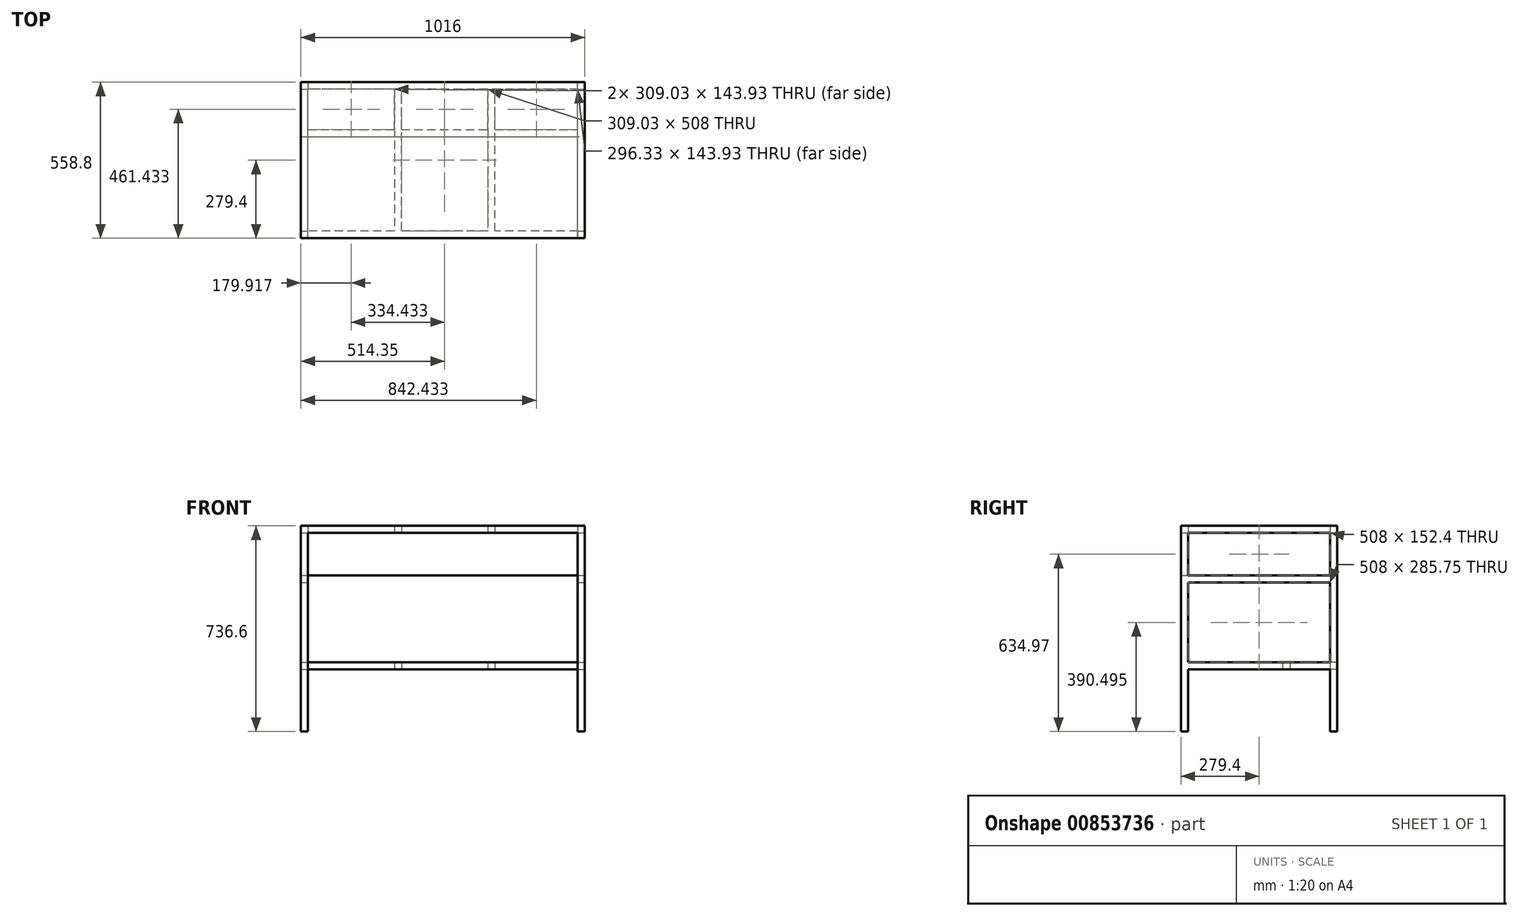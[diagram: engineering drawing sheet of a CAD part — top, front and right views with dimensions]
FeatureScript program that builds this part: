
annotation { "Feature Type Name" : "Feature", "Feature Type Description" : "" }
export const myFeature = defineFeature(function(context is Context, id is Id, definition is map)
    precondition{}
    {
        {
            assignVariable(context, id + "F0", {"name" : "width", "anyValue" : 1016 * mm});
        }
        {
            assignVariable(context, id + "F1", {"name" : "height", "anyValue" : 736.6 * mm});
        }
        {
            assignVariable(context, id + "F2", {"name" : "beam", "anyValue" : 25.4 * mm});
        }
        {
            assignVariable(context, id + "F3", {"name" : "ply", "anyValue" : 3 / 101.6 * mm});
        }
        {
            var Q0;
            Q0=qCreatedBy(makeId("Top.planeOp"),FACE);
            var sketch = newSketch(context, id + "F4", { "sketchPlane" : qUnion([Q0])});
            skLineSegment(sketch, "E0.bottom", {"start": v(508, -279.4) * mm, "end": v(-508, -279.4) * mm});
            skLineSegment(sketch, "E0.top", {"start": v(508, 279.4) * mm, "end": v(-508, 279.4) * mm});
            skLineSegment(sketch, "E0.left", {"start": v(508, -279.4) * mm, "end": v(508, 279.4) * mm});
            skLineSegment(sketch, "E0.right", {"start": v(-508, -279.4) * mm, "end": v(-508, 279.4) * mm});
            skPoint(sketch, "E0.middle", {"position": v(0, 0) * mm});
            skLineSegment(sketch, "E1.bottom", {"start": v(482.6, -254) * mm, "end": v(-482.6, -254) * mm});
            skLineSegment(sketch, "E1.top", {"start": v(482.6, 254) * mm, "end": v(-482.6, 254) * mm});
            skLineSegment(sketch, "E1.left", {"start": v(482.6, -254) * mm, "end": v(482.6, 254) * mm});
            skLineSegment(sketch, "E1.right", {"start": v(-482.6, -254) * mm, "end": v(-482.6, 254) * mm});
            skLineSegment(sketch, "E2", {"start": v(-173.57, 254) * mm, "end": v(-173.57, -254) * mm});
            skLineSegment(sketch, "E3", {"start": v(-173.57, -254) * mm, "end": v(-148.17, -254) * mm});
            skLineSegment(sketch, "E4", {"start": v(-148.17, -254) * mm, "end": v(-148.17, 254) * mm});
            skLineSegment(sketch, "E5", {"start": v(-148.17, 254) * mm, "end": v(-173.57, 254) * mm});
            skLineSegment(sketch, "E6", {"start": v(160.87, 254) * mm, "end": v(160.87, -254) * mm});
            skLineSegment(sketch, "E7", {"start": v(160.87, -254) * mm, "end": v(186.27, -254) * mm});
            skLineSegment(sketch, "E8", {"start": v(186.27, -254) * mm, "end": v(186.27, 254) * mm});
            skLineSegment(sketch, "E9", {"start": v(186.27, 254) * mm, "end": v(160.87, 254) * mm});
            skSolve(sketch);
        }
        {
            var Q0;
            Q0=makeQuery(id+"F4.imprint","IMPRINT",FACE,{"disambiguationData":[TD([[makeQuery(id+"F4.imprint","IMPRINT",EDGE,{"derivedFrom":sQuery(id+"F4.wireOp",EDGE,"E0.right")}),-1.0]])]});
            var Q1;
            Q1=makeQuery(id+"F4.imprint","IMPRINT",FACE,{"disambiguationData":[TD([[makeQuery(id+"F4.imprint","IMPRINT",EDGE,{"derivedFrom":sQuery(id+"F4.wireOp",EDGE,"E0.bottom")}),-1.0]])]});
            var Q2;
            Q2=makeQuery(id+"F4.imprint","IMPRINT",FACE,{"disambiguationData":[TD([[makeQuery(id+"F4.imprint","IMPRINT",EDGE,{"derivedFrom":sQuery(id+"F4.wireOp",EDGE,"E0.top")}),1.0]])]});
            var Q3;
            Q3=makeQuery(id+"F4.imprint","IMPRINT",FACE,{"disambiguationData":[TD([[makeQuery(id+"F4.imprint","IMPRINT",EDGE,{"derivedFrom":sQuery(id+"F4.wireOp",EDGE,"E0.left")}),1.0]])]});
            var Q4;
            Q4=makeQuery(id+"F4.imprint","IMPRINT",FACE,{"disambiguationData":[TD([[makeQuery(id+"F4.imprint","IMPRINT",EDGE,{"derivedFrom":sQuery(id+"F4.wireOp",EDGE,"E2")}),1.0]])]});
            var Q5;
            Q5=makeQuery(id+"F4.imprint","IMPRINT",FACE,{"disambiguationData":[TD([[makeQuery(id+"F4.imprint","IMPRINT",EDGE,{"derivedFrom":sQuery(id+"F4.wireOp",EDGE,"E6")}),1.0]])]});
            extrude(context, id + "F5", {"entities" : qUnion([Q0, Q1, Q2, Q3, Q4, Q5]), "depth" : getVariable(context, 'beam'), "offsetDistance" : 25.4 * mm});
        }
        {
            var Q0;
            Q0=makeQuery(id+"F5.opExtrude","CAP_FACE",FACE,{"disambiguationData":[OSD([sQuery(id+"F4.wireOp",EDGE,"E0.bottom"),sQuery(id+"F4.wireOp",EDGE,"E0.top"),sQuery(id+"F4.wireOp",EDGE,"E0.left"),sQuery(id+"F4.wireOp",EDGE,"E0.right"),sQuery(id+"F4.wireOp",EDGE,"E1.bottom"),sQuery(id+"F4.wireOp",EDGE,"E1.top"),sQuery(id+"F4.wireOp",EDGE,"E1.left"),sQuery(id+"F4.wireOp",EDGE,"E1.right")])],"isStart":false});
            var sketch = newSketch(context, id + "F6", { "sketchPlane" : qUnion([Q0])});
            skLineSegment(sketch, "E10.bottom", {"start": v(-508, 279.4) * mm, "end": v(508, 279.4) * mm});
            skLineSegment(sketch, "E10.top", {"start": v(-508, -279.4) * mm, "end": v(508, -279.4) * mm});
            skLineSegment(sketch, "E10.left", {"start": v(-508, 279.4) * mm, "end": v(-508, -279.4) * mm});
            skLineSegment(sketch, "E10.right", {"start": v(508, 279.4) * mm, "end": v(508, -279.4) * mm});
            skSolve(sketch);
        }
        {
            var Q0;
            Q0 = qSketchRegion(id + "F6", true);
            extrude(context, id + "F7", {"entities" : qUnion([Q0]), "depth" : getVariable(context, 'ply'), "offsetDistance" : 25.4 * mm});
        }
        {
            var Q0;
            Q0=makeQuery(id+"F5.opExtrude","CAP_FACE",FACE,{"disambiguationData":[OSD([sQuery(id+"F4.wireOp",EDGE,"E0.bottom"),sQuery(id+"F4.wireOp",EDGE,"E0.top"),sQuery(id+"F4.wireOp",EDGE,"E0.left"),sQuery(id+"F4.wireOp",EDGE,"E0.right"),sQuery(id+"F4.wireOp",EDGE,"E1.bottom"),sQuery(id+"F4.wireOp",EDGE,"E1.top"),sQuery(id+"F4.wireOp",EDGE,"E1.left"),sQuery(id+"F4.wireOp",EDGE,"E1.right"),sQuery(id+"F4.wireOp",EDGE,"E2"),sQuery(id+"F4.wireOp",EDGE,"E4"),sQuery(id+"F4.wireOp",EDGE,"E6"),sQuery(id+"F4.wireOp",EDGE,"E8")])],"isStart":true});
            var sketch = newSketch(context, id + "F8", { "sketchPlane" : qUnion([Q0])});
            skLineSegment(sketch, "E11.bottom", {"start": v(-508, 279.4) * mm, "end": v(-482.6, 279.4) * mm});
            skLineSegment(sketch, "E11.top", {"start": v(-508, 254) * mm, "end": v(-482.6, 254) * mm});
            skLineSegment(sketch, "E11.left", {"start": v(-508, 279.4) * mm, "end": v(-508, 254) * mm});
            skLineSegment(sketch, "E11.right", {"start": v(-482.6, 279.4) * mm, "end": v(-482.6, 254) * mm});
            skLineSegment(sketch, "E12.bottom", {"start": v(-508, -279.4) * mm, "end": v(-482.6, -279.4) * mm});
            skLineSegment(sketch, "E12.top", {"start": v(-508, -254) * mm, "end": v(-482.6, -254) * mm});
            skLineSegment(sketch, "E12.left", {"start": v(-508, -279.4) * mm, "end": v(-508, -254) * mm});
            skLineSegment(sketch, "E12.right", {"start": v(-482.6, -279.4) * mm, "end": v(-482.6, -254) * mm});
            skLineSegment(sketch, "E13.bottom", {"start": v(482.6, 254) * mm, "end": v(508, 254) * mm});
            skLineSegment(sketch, "E13.top", {"start": v(482.6, 279.4) * mm, "end": v(508, 279.4) * mm});
            skLineSegment(sketch, "E13.left", {"start": v(482.6, 254) * mm, "end": v(482.6, 279.4) * mm});
            skLineSegment(sketch, "E13.right", {"start": v(508, 254) * mm, "end": v(508, 279.4) * mm});
            skLineSegment(sketch, "E14.bottom", {"start": v(482.6, -254) * mm, "end": v(508, -254) * mm});
            skLineSegment(sketch, "E14.top", {"start": v(482.6, -279.4) * mm, "end": v(508, -279.4) * mm});
            skLineSegment(sketch, "E14.left", {"start": v(482.6, -254) * mm, "end": v(482.6, -279.4) * mm});
            skLineSegment(sketch, "E14.right", {"start": v(508, -254) * mm, "end": v(508, -279.4) * mm});
            skSolve(sketch);
        }
        {
            var Q0;
            Q0 = qSketchRegion(id + "F8", true);
            extrude(context, id + "F9", {"entities" : qUnion([Q0]), "operationType" : NewBodyOperationType.ADD, "depth" : getVariable(context, 'height') - getVariable(context, 'beam') - getVariable(context, 'ply'), "offsetDistance" : 25.4 * mm});
        }
        {
            var Q0;
            Q0=makeQuery(id+"F9.opExtrude","SWEPT_FACE",FACE,{"disambiguationData":[OSD([sQuery(id+"F8.wireOp",EDGE,"E12.top")])]});
            var sketch = newSketch(context, id + "F10", { "sketchPlane" : qUnion([Q0])});
            skLineSegment(sketch, "E15.bottom", {"start": v(-508, -463.55) * mm, "end": v(-482.6, -463.55) * mm});
            skLineSegment(sketch, "E15.top", {"start": v(-508, -488.95) * mm, "end": v(-482.6, -488.95) * mm});
            skLineSegment(sketch, "E15.left", {"start": v(-508, -463.55) * mm, "end": v(-508, -488.95) * mm});
            skLineSegment(sketch, "E15.right", {"start": v(-482.6, -463.55) * mm, "end": v(-482.6, -488.95) * mm});
            skSolve(sketch);
        }
        {
            var Q0;
            Q0=makeQuery(id+"F10.imprint","IMPRINT",FACE,{"disambiguationData":[TD([[makeQuery(id+"F10.imprint","IMPRINT",EDGE,{"derivedFrom":sQuery(id+"F10.wireOp",EDGE,"E15.bottom")}),-1.0]])]});
            extrude(context, id + "F11", {"entities" : qUnion([Q0]), "operationType" : NewBodyOperationType.ADD, "endBound" : BoundingType.UP_TO_NEXT, "depth" : 25.4 * mm, "offsetDistance" : 25.4 * mm});
        }
        {
            var Q0;
            Q0=makeQuery(id+"F9.opExtrude","SWEPT_FACE",FACE,{"disambiguationData":[OSD([sQuery(id+"F8.wireOp",EDGE,"E14.bottom")])]});
            var sketch = newSketch(context, id + "F12", { "sketchPlane" : qUnion([Q0])});
            skLineSegment(sketch, "E16.bottom", {"start": v(482.6, -463.55) * mm, "end": v(508, -463.55) * mm});
            skLineSegment(sketch, "E16.top", {"start": v(482.6, -488.95) * mm, "end": v(508, -488.95) * mm});
            skLineSegment(sketch, "E16.left", {"start": v(482.6, -463.55) * mm, "end": v(482.6, -488.95) * mm});
            skLineSegment(sketch, "E16.right", {"start": v(508, -463.55) * mm, "end": v(508, -488.95) * mm});
            skSolve(sketch);
        }
        {
            var Q0;
            Q0=makeQuery(id+"F12.imprint","IMPRINT",FACE,{"disambiguationData":[TD([[makeQuery(id+"F12.imprint","IMPRINT",EDGE,{"derivedFrom":sQuery(id+"F12.wireOp",EDGE,"E16.bottom")}),-1.0]])]});
            extrude(context, id + "F13", {"entities" : qUnion([Q0]), "operationType" : NewBodyOperationType.ADD, "endBound" : BoundingType.UP_TO_NEXT, "depth" : 25.4 * mm, "offsetDistance" : 25.4 * mm});
        }
        {
            var Q0;
            Q0=makeQuery(id+"F13.boolean.opBoolean","MERGE",FACE,{"derivedFrom":[makeQuery(id+"F9.opExtrude","SWEPT_FACE",FACE,{"disambiguationData":[OSD([sQuery(id+"F8.wireOp",EDGE,"E13.left")])]}),makeQuery(id+"F9.opExtrude","SWEPT_FACE",FACE,{"disambiguationData":[OSD([sQuery(id+"F8.wireOp",EDGE,"E14.left")])]}),makeQuery(id+"F13.opExtrude","SWEPT_FACE",FACE,{"disambiguationData":[OSD([sQuery(id+"F12.wireOp",EDGE,"E16.left")])]})]});
            var sketch = newSketch(context, id + "F14", { "sketchPlane" : qUnion([Q0])});
            skLineSegment(sketch, "E17.bottom", {"start": v(-110.07, -463.55) * mm, "end": v(-84.67, -463.55) * mm});
            skLineSegment(sketch, "E17.top", {"start": v(-110.07, -488.95) * mm, "end": v(-84.67, -488.95) * mm});
            skLineSegment(sketch, "E17.left", {"start": v(-110.07, -463.55) * mm, "end": v(-110.07, -488.95) * mm});
            skLineSegment(sketch, "E17.right", {"start": v(-84.67, -463.55) * mm, "end": v(-84.67, -488.95) * mm});
            skLineSegment(sketch, "E18.bottom", {"start": v(-254, -463.55) * mm, "end": v(-279.4, -463.55) * mm});
            skLineSegment(sketch, "E18.top", {"start": v(-254, -488.95) * mm, "end": v(-279.4, -488.95) * mm});
            skLineSegment(sketch, "E18.left", {"start": v(-254, -463.55) * mm, "end": v(-254, -488.95) * mm});
            skLineSegment(sketch, "E18.right", {"start": v(-279.4, -463.55) * mm, "end": v(-279.4, -488.95) * mm});
            skSolve(sketch);
        }
        {
            var Q0;
            Q0=makeQuery(id+"F14.imprint","IMPRINT",FACE,{"disambiguationData":[TD([[makeQuery(id+"F14.imprint","IMPRINT",EDGE,{"derivedFrom":sQuery(id+"F14.wireOp",EDGE,"E17.bottom")}),1.0]])]});
            var Q1;
            Q1=makeQuery(id+"F14.imprint","IMPRINT",FACE,{"disambiguationData":[TD([[makeQuery(id+"F14.imprint","IMPRINT",EDGE,{"derivedFrom":sQuery(id+"F14.wireOp",EDGE,"E18.bottom")}),1.0]])]});
            extrude(context, id + "F15", {"entities" : qUnion([Q0, Q1]), "operationType" : NewBodyOperationType.ADD, "endBound" : BoundingType.UP_TO_NEXT, "depth" : 25.4 * mm, "offsetDistance" : 25.4 * mm});
        }
        {
            var Q0;
            Q0=makeQuery(id+"F15.opExtrude","SWEPT_FACE",FACE,{"disambiguationData":[OSD([sQuery(id+"F14.wireOp",EDGE,"E18.left")])]});
            var sketch = newSketch(context, id + "F16", { "sketchPlane" : qUnion([Q0])});
            skLineSegment(sketch, "E19.bottom", {"start": v(-173.57, -463.55) * mm, "end": v(-148.17, -463.55) * mm});
            skLineSegment(sketch, "E19.top", {"start": v(-173.57, -488.95) * mm, "end": v(-148.17, -488.95) * mm});
            skLineSegment(sketch, "E19.left", {"start": v(-173.57, -463.55) * mm, "end": v(-173.57, -488.95) * mm});
            skLineSegment(sketch, "E19.right", {"start": v(-148.17, -463.55) * mm, "end": v(-148.17, -488.95) * mm});
            skLineSegment(sketch, "E20.bottom", {"start": v(160.87, -463.55) * mm, "end": v(186.27, -463.55) * mm});
            skLineSegment(sketch, "E20.top", {"start": v(160.87, -488.95) * mm, "end": v(186.27, -488.95) * mm});
            skLineSegment(sketch, "E20.left", {"start": v(160.87, -463.55) * mm, "end": v(160.87, -488.95) * mm});
            skLineSegment(sketch, "E20.right", {"start": v(186.27, -463.55) * mm, "end": v(186.27, -488.95) * mm});
            skSolve(sketch);
        }
        {
            var Q0;
            Q0=makeQuery(id+"F16.imprint","IMPRINT",FACE,{"disambiguationData":[TD([[makeQuery(id+"F16.imprint","IMPRINT",EDGE,{"derivedFrom":sQuery(id+"F16.wireOp",EDGE,"E19.bottom")}),-1.0]])]});
            var Q1;
            Q1=makeQuery(id+"F16.imprint","IMPRINT",FACE,{"disambiguationData":[TD([[makeQuery(id+"F16.imprint","IMPRINT",EDGE,{"derivedFrom":sQuery(id+"F16.wireOp",EDGE,"E20.bottom")}),-1.0]])]});
            extrude(context, id + "F17", {"entities" : qUnion([Q0, Q1]), "operationType" : NewBodyOperationType.ADD, "endBound" : BoundingType.UP_TO_NEXT, "depth" : 25.4 * mm, "offsetDistance" : 25.4 * mm});
        }
        {
            var Q0;
            Q0=makeQuery(id+"F17.boolean.opBoolean","MERGE",FACE,{"derivedFrom":[makeQuery(id+"F15.opExtrude","SWEPT_FACE",FACE,{"disambiguationData":[OSD([sQuery(id+"F14.wireOp",EDGE,"E18.bottom")])]}),makeQuery(id+"F15.boolean.opBoolean","MERGE",FACE,{"derivedFrom":[makeQuery(id+"F11.opExtrude","SWEPT_FACE",FACE,{"disambiguationData":[OSD([sQuery(id+"F10.wireOp",EDGE,"E15.bottom")])]}),makeQuery(id+"F13.opExtrude","SWEPT_FACE",FACE,{"disambiguationData":[OSD([sQuery(id+"F12.wireOp",EDGE,"E16.bottom")])]}),makeQuery(id+"F15.opExtrude","SWEPT_FACE",FACE,{"disambiguationData":[OSD([sQuery(id+"F14.wireOp",EDGE,"E17.bottom")])]})]}),makeQuery(id+"F17.opExtrude","SWEPT_FACE",FACE,{"disambiguationData":[OSD([sQuery(id+"F16.wireOp",EDGE,"E19.bottom")])]}),makeQuery(id+"F17.opExtrude","SWEPT_FACE",FACE,{"disambiguationData":[OSD([sQuery(id+"F16.wireOp",EDGE,"E20.bottom")])]})]});
            var sketch = newSketch(context, id + "F18", { "sketchPlane" : qUnion([Q0])});
            skLineSegment(sketch, "E21", {"start": v(-508, 254) * mm, "end": v(-482.6, 254) * mm});
            skLineSegment(sketch, "E22", {"start": v(-482.6, 254) * mm, "end": v(-482.6, 279.4) * mm});
            skLineSegment(sketch, "E23", {"start": v(-482.6, 279.4) * mm, "end": v(482.6, 279.4) * mm});
            skLineSegment(sketch, "E24", {"start": v(482.6, 279.4) * mm, "end": v(482.6, 254) * mm});
            skLineSegment(sketch, "E25", {"start": v(482.6, 254) * mm, "end": v(508, 254) * mm});
            skLineSegment(sketch, "E26", {"start": v(-508, 254) * mm, "end": v(-508, 84.67) * mm});
            skLineSegment(sketch, "E27", {"start": v(-508, 84.67) * mm, "end": v(508, 84.67) * mm});
            skLineSegment(sketch, "E28", {"start": v(508, 84.67) * mm, "end": v(508, 254) * mm});
            skSolve(sketch);
        }
        {
            var Q0;
            Q0 = qSketchRegion(id + "F18", true);
            extrude(context, id + "F19", {"entities" : qUnion([Q0]), "depth" : getVariable(context, 'ply'), "offsetDistance" : 25.4 * mm});
        }
        {
            var Q0;
            {var subQ0=sQuery(id+"F4.wireOp",EDGE,"E1.right");Q0=makeQuery(id+"F11.boolean.opBoolean","SPLIT",FACE,{"disambiguationData":[TD([makeQuery(id+"F5.opExtrude","SWEPT_FACE",FACE,{"disambiguationData":[OSD([subQ0])]})])],"derivedFrom":makeQuery(id+"F9.opExtrude","SWEPT_FACE",FACE,{"disambiguationData":[OSD([sQuery(id+"F8.wireOp",EDGE,"E12.top")])]})});}
            var sketch = newSketch(context, id + "F20", { "sketchPlane" : qUnion([Q0])});
            skLineSegment(sketch, "E29.bottom", {"start": v(-508, -152.4) * mm, "end": v(-482.6, -152.4) * mm});
            skLineSegment(sketch, "E29.top", {"start": v(-508, -177.8) * mm, "end": v(-482.6, -177.8) * mm});
            skLineSegment(sketch, "E29.left", {"start": v(-508, -152.4) * mm, "end": v(-508, -177.8) * mm});
            skLineSegment(sketch, "E29.right", {"start": v(-482.6, -152.4) * mm, "end": v(-482.6, -177.8) * mm});
            skSolve(sketch);
        }
        {
            var Q0;
            Q0=makeQuery(id+"F20.imprint","IMPRINT",FACE,{"disambiguationData":[TD([[makeQuery(id+"F20.imprint","IMPRINT",EDGE,{"derivedFrom":sQuery(id+"F20.wireOp",EDGE,"E29.bottom")}),-1.0]])]});
            extrude(context, id + "F21", {"entities" : qUnion([Q0]), "operationType" : NewBodyOperationType.ADD, "endBound" : BoundingType.UP_TO_NEXT, "depth" : 25.4 * mm, "offsetDistance" : 25.4 * mm});
        }
        {
            var Q0;
            {var subQ1=sQuery(id+"F4.wireOp",EDGE,"E1.left");Q0=makeQuery(id+"F13.boolean.opBoolean","SPLIT",FACE,{"disambiguationData":[TD([makeQuery(id+"F5.opExtrude","SWEPT_FACE",FACE,{"disambiguationData":[OSD([subQ1])]})])],"derivedFrom":makeQuery(id+"F9.opExtrude","SWEPT_FACE",FACE,{"disambiguationData":[OSD([sQuery(id+"F8.wireOp",EDGE,"E14.bottom")])]})});}
            var sketch = newSketch(context, id + "F22", { "sketchPlane" : qUnion([Q0])});
            skLineSegment(sketch, "E30.bottom", {"start": v(482.6, -152.4) * mm, "end": v(508, -152.4) * mm});
            skLineSegment(sketch, "E30.top", {"start": v(482.6, -177.8) * mm, "end": v(508, -177.8) * mm});
            skLineSegment(sketch, "E30.left", {"start": v(482.6, -152.4) * mm, "end": v(482.6, -177.8) * mm});
            skLineSegment(sketch, "E30.right", {"start": v(508, -152.4) * mm, "end": v(508, -177.8) * mm});
            skSolve(sketch);
        }
        {
            var Q0;
            Q0=makeQuery(id+"F22.imprint","IMPRINT",FACE,{"disambiguationData":[TD([[makeQuery(id+"F22.imprint","IMPRINT",EDGE,{"derivedFrom":sQuery(id+"F22.wireOp",EDGE,"E30.bottom")}),-1.0]])]});
            extrude(context, id + "F23", {"entities" : qUnion([Q0]), "operationType" : NewBodyOperationType.ADD, "endBound" : BoundingType.UP_TO_NEXT, "depth" : 25.4 * mm, "offsetDistance" : 25.4 * mm});
        }
        {
            var Q0;
            {var subQ1=sQuery(id+"F4.wireOp",EDGE,"E1.right");var subQ2=sQuery(id+"F4.wireOp",EDGE,"E1.top");var subQ5=sQuery(id+"F4.wireOp",EDGE,"E0.bottom");var subQ11=sQuery(id+"F8.wireOp",EDGE,"E11.right");var subQ14=makeQuery(id+"F11.opExtrude","SWEPT_FACE",FACE,{"disambiguationData":[OSD([sQuery(id+"F10.wireOp",EDGE,"E15.right")])]});var subQ15=makeQuery(id+"F9.opExtrude","SWEPT_FACE",FACE,{"disambiguationData":[OSD([sQuery(id+"F8.wireOp",EDGE,"E12.right")])]});var subQ16=makeQuery(id+"F9.opExtrude","SWEPT_FACE",FACE,{"disambiguationData":[OSD([subQ11])]});var subQ17=makeQuery(id+"F11.boolean.opBoolean","MERGE",FACE,{"derivedFrom":[subQ16,subQ15,subQ14]});Q0=makeQuery(id+"F21.boolean.opBoolean","MERGE",FACE,{"derivedFrom":[makeQuery(id+"F15.boolean.opBoolean","SPLIT",FACE,{"disambiguationData":[TD([makeQuery(id+"F5.opExtrude","SWEPT_FACE",FACE,{"disambiguationData":[OSD([subQ2]),TDD([makeQuery(id+"F4.imprint","IMPRINT",EDGE,{"disambiguationData":[TD([[makeQuery(id+"F4.imprint","INTERSECT",VERTEX,{"derivedFrom":[subQ2,subQ1]}),1.0]])],"derivedFrom":subQ2})])]})])],"derivedFrom":subQ17}),makeQuery(id+"F15.boolean.opBoolean","SPLIT",FACE,{"disambiguationData":[TD([makeQuery(id+"F5.opExtrude","SWEPT_FACE",FACE,{"disambiguationData":[OSD([subQ5])]})])],"derivedFrom":subQ17}),makeQuery(id+"F21.opExtrude","SWEPT_FACE",FACE,{"disambiguationData":[OSD([sQuery(id+"F20.wireOp",EDGE,"E29.right")])]})]});}
            var sketch = newSketch(context, id + "F24", { "sketchPlane" : qUnion([Q0])});
            skLineSegment(sketch, "E31.bottom", {"start": v(-279.4, 0) * mm, "end": v(254, 0) * mm});
            skLineSegment(sketch, "E31.top", {"start": v(-279.4, -152.4) * mm, "end": v(254, -152.4) * mm});
            skLineSegment(sketch, "E31.left", {"start": v(-279.4, 0) * mm, "end": v(-279.4, -152.4) * mm});
            skLineSegment(sketch, "E31.right", {"start": v(254, 0) * mm, "end": v(254, -152.4) * mm});
            skSolve(sketch);
        }
        {
            var Q0;
            {var subQ15=sQuery(id+"F24.wireOp",EDGE,"E31.right");Q0=makeQuery(id+"F24.imprint","IMPRINT",FACE,{"disambiguationData":[TD([[makeQuery(id+"F24.imprint","IMPRINT",EDGE,{"derivedFrom":subQ15}),1.0]])]});}
            var Q1;
            {var subQ15=sQuery(id+"F24.wireOp",EDGE,"E31.left");Q1=makeQuery(id+"F24.imprint","IMPRINT",FACE,{"disambiguationData":[TD([[makeQuery(id+"F24.imprint","IMPRINT",EDGE,{"derivedFrom":subQ15}),-1.0]])]});}
            extrude(context, id + "F25", {"entities" : qUnion([Q0, Q1]), "depth" : getVariable(context, 'width') - 2 * getVariable(context, 'beam'), "offsetDistance" : 25.4 * mm});
        }
    });
